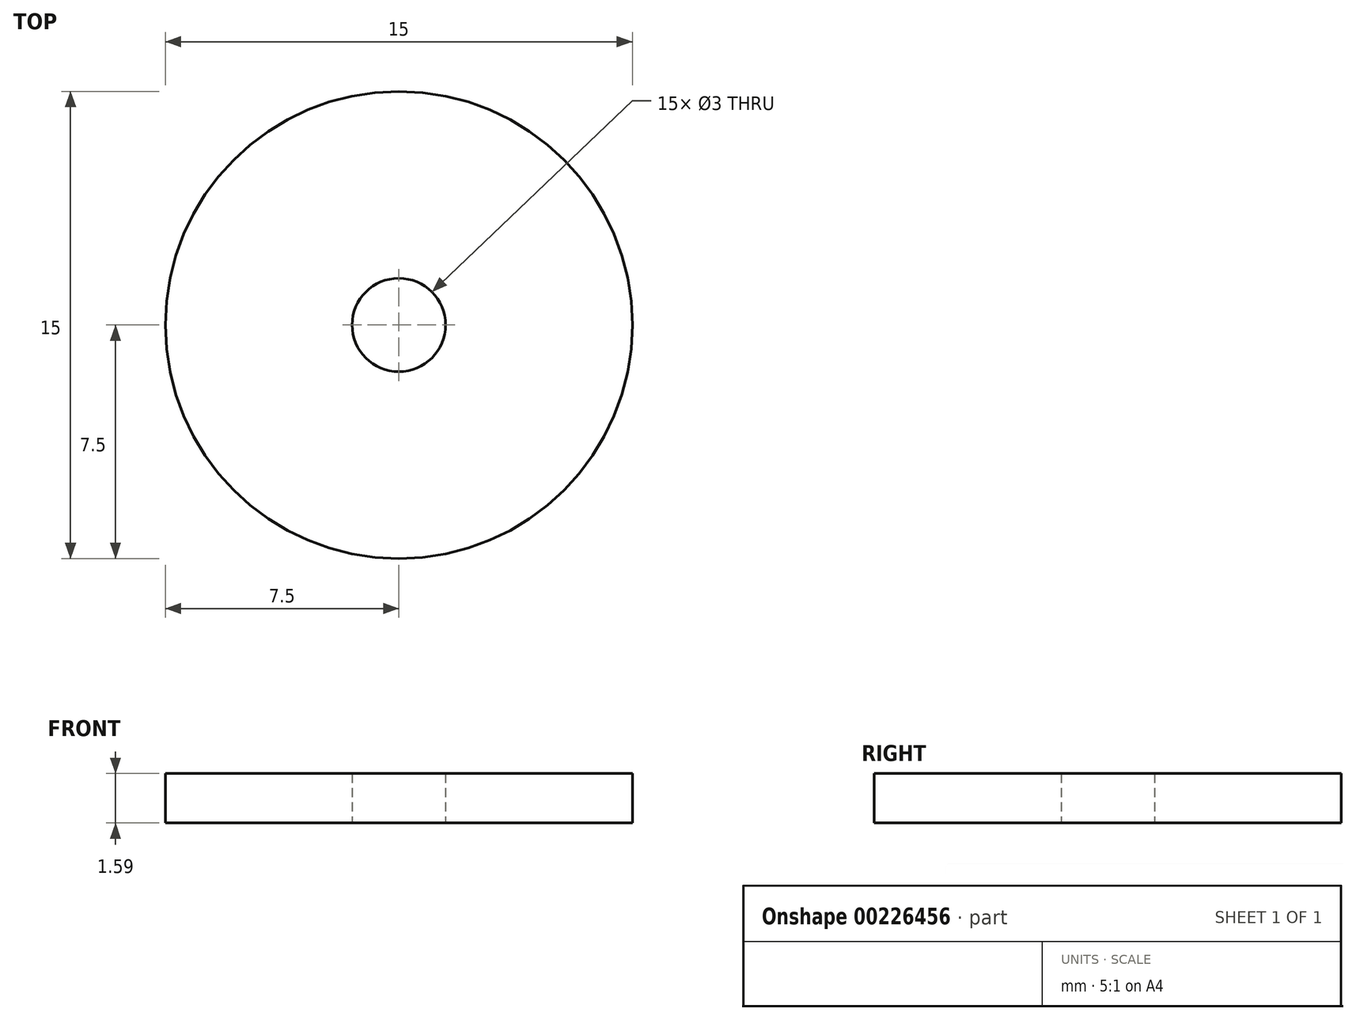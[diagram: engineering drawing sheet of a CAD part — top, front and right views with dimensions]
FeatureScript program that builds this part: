
annotation { "Feature Type Name" : "Feature", "Feature Type Description" : "" }
export const myFeature = defineFeature(function(context is Context, id is Id, definition is map)
    precondition{}
    {
        {
            var Q0;
            Q0=qCreatedBy(makeId("Top.planeOp"),FACE);
            var sketch = newSketch(context, id + "F0", { "sketchPlane" : qUnion([Q0])});
            skCircle(sketch, "E0", {"center": v(0, 0) * mm, "radius": 7.5 * mm});
            skCircle(sketch, "E1", {"center": v(0, 0) * mm, "radius": 1.5 * mm});
            skSolve(sketch);
        }
        {
            var Q0;
            Q0 = qSketchRegion(id + "F0", true);
            extrude(context, id + "F1", {"entities" : qUnion([Q0]), "depth" : 1.59 * mm});
        }
    });
